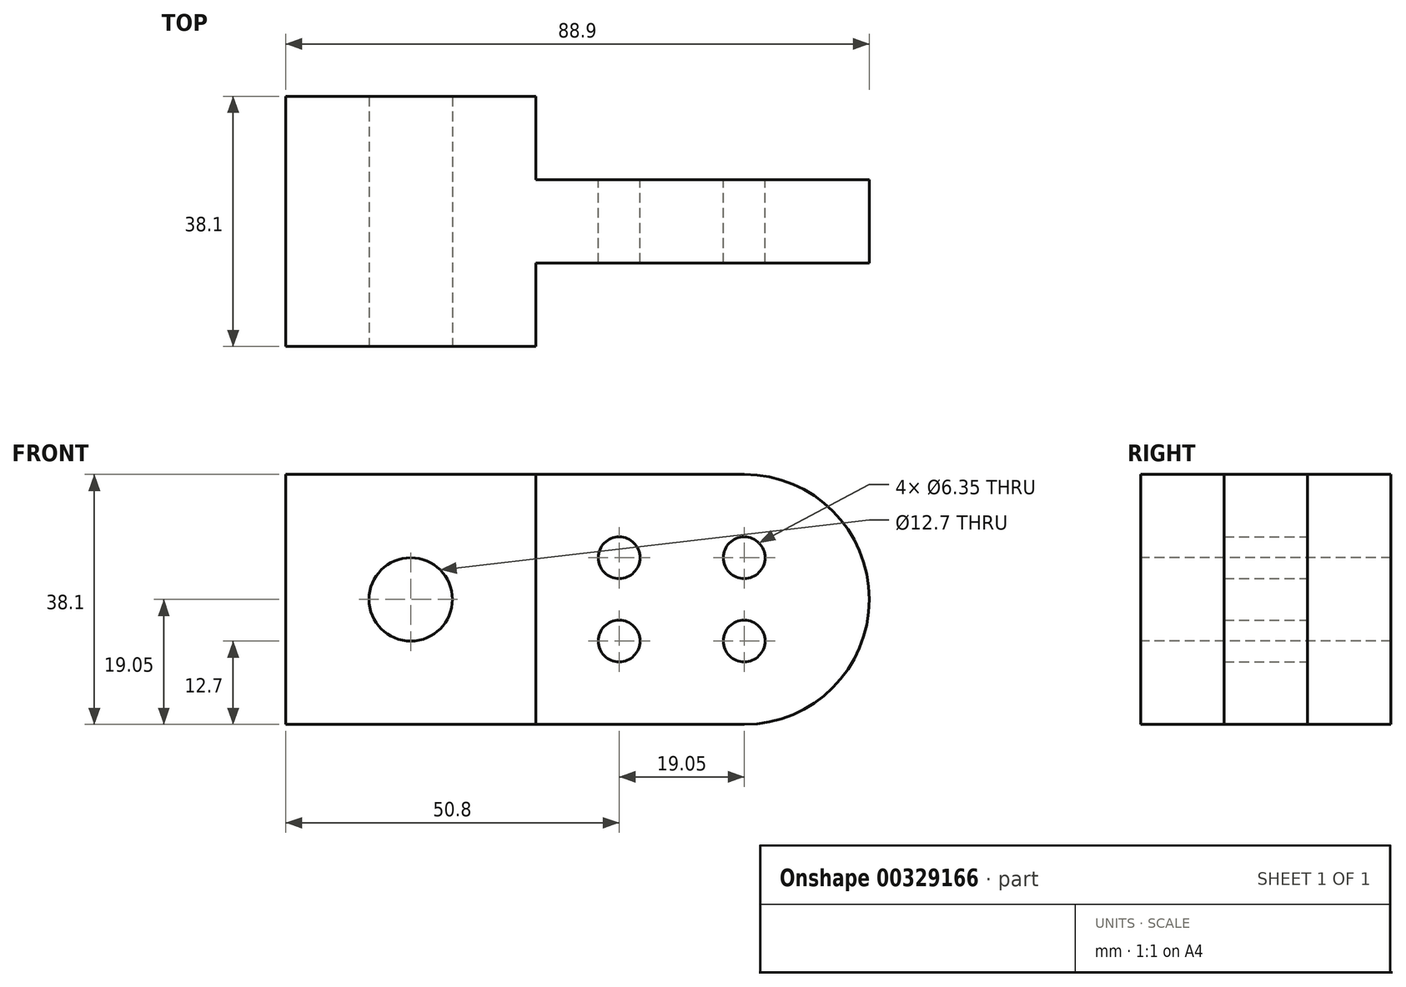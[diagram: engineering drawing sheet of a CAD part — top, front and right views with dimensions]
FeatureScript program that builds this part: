
annotation { "Feature Type Name" : "Feature", "Feature Type Description" : "" }
export const myFeature = defineFeature(function(context is Context, id is Id, definition is map)
    precondition{}
    {
        {
            var Q0;
            Q0=qCreatedBy(makeId("Front.planeOp"),FACE);
            var sketch = newSketch(context, id + "F0", { "sketchPlane" : qUnion([Q0])});
            skLineSegment(sketch, "E0", {"start": v(0, 0) * mm, "end": v(0, 38.1) * mm});
            skLineSegment(sketch, "E1", {"start": v(0, 38.1) * mm, "end": v(38.1, 38.1) * mm});
            skLineSegment(sketch, "E2", {"start": v(38.1, 38.1) * mm, "end": v(38.1, 0) * mm});
            skLineSegment(sketch, "E3", {"start": v(38.1, 0) * mm, "end": v(0, 0) * mm});
            skLineSegment(sketch, "E4", {"start": v(38.1, 38.1) * mm, "end": v(69.85, 38.1) * mm});
            skLineSegment(sketch, "E5", {"start": v(38.1, 0) * mm, "end": v(69.85, 0) * mm});
            skArc(sketch, "E6", {"start": v(69.85, 0) * mm, "mid": v(88.9, 19.05) * mm, "end": v(69.85, 38.1) * mm});
            skLineSegment(sketch, "E7", {"start": v(38.1, 25.4) * mm, "end": v(109.02, 25.4) * mm, "construction": true});
            skLineSegment(sketch, "E8", {"start": v(38.1, 12.7) * mm, "end": v(109.02, 12.7) * mm, "construction": true});
            skLineSegment(sketch, "E9", {"start": v(38.1, 19.05) * mm, "end": v(88.9, 19.05) * mm});
            skLineSegment(sketch, "E10", {"start": v(50.8, 38.1) * mm, "end": v(50.8, 0) * mm, "construction": true});
            skLineSegment(sketch, "E11", {"start": v(69.85, 38.1) * mm, "end": v(69.85, 0) * mm, "construction": true});
            skCircle(sketch, "E12", {"center": v(50.8, 25.4) * mm, "radius": 3.18 * mm});
            skCircle(sketch, "E13", {"center": v(69.85, 25.4) * mm, "radius": 3.18 * mm});
            skCircle(sketch, "E14", {"center": v(69.85, 12.7) * mm, "radius": 3.18 * mm});
            skCircle(sketch, "E15", {"center": v(50.8, 12.7) * mm, "radius": 3.18 * mm});
            skSolve(sketch);
        }
        {
            var Q0;
            Q0=makeQuery(id+"F0.imprint","IMPRINT",FACE,{"disambiguationData":[TD([[makeQuery(id+"F0.imprint","IMPRINT",EDGE,{"derivedFrom":sQuery(id+"F0.wireOp",EDGE,"E0")}),-1.0]])]});
            var Q1;
            {var subQ2=sQuery(id+"F0.wireOp",EDGE,"E4");Q1=makeQuery(id+"F0.imprint","IMPRINT",FACE,{"disambiguationData":[TD([[makeQuery(id+"F0.imprint","IMPRINT",EDGE,{"derivedFrom":subQ2}),-1.0]])]});}
            var Q2;
            {var subQ2=sQuery(id+"F0.wireOp",EDGE,"E5");Q2=makeQuery(id+"F0.imprint","IMPRINT",FACE,{"disambiguationData":[TD([[makeQuery(id+"F0.imprint","IMPRINT",EDGE,{"derivedFrom":subQ2}),1.0]])]});}
            extrude(context, id + "F1", {"entities" : qUnion([Q0, Q1, Q2]), "depth" : 38.1 * mm});
        }
        {
            var Q0;
            Q0=qCreatedBy(makeId("Top.planeOp"),FACE);
            var sketch = newSketch(context, id + "F2", { "sketchPlane" : qUnion([Q0])});
            skLineSegment(sketch, "E16", {"start": v(0, 0) * mm, "end": v(38.1, 0) * mm});
            skLineSegment(sketch, "E17", {"start": v(38.1, 0) * mm, "end": v(38.1, -12.7) * mm});
            skLineSegment(sketch, "E18", {"start": v(38.1, -12.7) * mm, "end": v(88.9, -12.7) * mm});
            skLineSegment(sketch, "E19", {"start": v(88.9, -12.7) * mm, "end": v(88.9, -25.4) * mm});
            skLineSegment(sketch, "E20", {"start": v(88.9, -25.4) * mm, "end": v(38.1, -25.4) * mm});
            skLineSegment(sketch, "E21", {"start": v(38.1, -25.4) * mm, "end": v(38.1, -38.1) * mm});
            skLineSegment(sketch, "E22", {"start": v(38.1, -38.1) * mm, "end": v(0, -38.1) * mm});
            skLineSegment(sketch, "E23", {"start": v(0, -38.1) * mm, "end": v(0, 0) * mm});
            skLineSegment(sketch, "E24", {"start": v(38.1, -38.1) * mm, "end": v(88.9, -38.1) * mm});
            skLineSegment(sketch, "E25", {"start": v(88.9, -12.7) * mm, "end": v(88.9, 0) * mm});
            skLineSegment(sketch, "E26", {"start": v(88.9, 0) * mm, "end": v(38.1, 0) * mm});
            skLineSegment(sketch, "E27", {"start": v(88.9, -38.1) * mm, "end": v(88.9, -25.4) * mm});
            skSolve(sketch);
        }
        {
            var Q0;
            Q0=makeQuery(id+"F2.imprint","IMPRINT",FACE,{"disambiguationData":[TD([[makeQuery(id+"F2.imprint","IMPRINT",EDGE,{"derivedFrom":sQuery(id+"F2.wireOp",EDGE,"E17")}),1.0]])]});
            var Q1;
            Q1=makeQuery(id+"F2.imprint","IMPRINT",FACE,{"disambiguationData":[TD([[makeQuery(id+"F2.imprint","IMPRINT",EDGE,{"derivedFrom":sQuery(id+"F2.wireOp",EDGE,"E20")}),1.0]])]});
            var Q2;
            Q2=makeQuery(id+"F2.imprint","IMPRINT",FACE,{"disambiguationData":[TD([[makeQuery(id+"F2.imprint","IMPRINT",EDGE,{"derivedFrom":sQuery(id+"F2.wireOp",EDGE,"E17")}),1.0]])]});
            var Q3;
            Q3=makeQuery(id+"F2.imprint","IMPRINT",FACE,{"disambiguationData":[TD([[makeQuery(id+"F2.imprint","IMPRINT",EDGE,{"derivedFrom":sQuery(id+"F2.wireOp",EDGE,"E20")}),1.0]])]});
            extrude(context, id + "F3", {"entities" : qUnion([Q0, Q1, Q2, Q3]), "operationType" : NewBodyOperationType.REMOVE, "endBound" : BoundingType.THROUGH_ALL, "depth" : 25.4 * mm});
        }
        {
            var Q0;
            Q0=makeQuery(id+"F1.opExtrude","CAP_FACE",FACE,{"disambiguationData":[OSD([sQuery(id+"F0.wireOp",EDGE,"E0"),sQuery(id+"F0.wireOp",EDGE,"E1"),sQuery(id+"F0.wireOp",EDGE,"E3"),sQuery(id+"F0.wireOp",EDGE,"E4"),sQuery(id+"F0.wireOp",EDGE,"E5"),sQuery(id+"F0.wireOp",EDGE,"E6"),sQuery(id+"F0.wireOp",EDGE,"E12"),sQuery(id+"F0.wireOp",EDGE,"E13"),sQuery(id+"F0.wireOp",EDGE,"E14"),sQuery(id+"F0.wireOp",EDGE,"E15")])],"isStart":false});
            var sketch = newSketch(context, id + "F4", { "sketchPlane" : qUnion([Q0])});
            skCircle(sketch, "E28", {"center": v(19.05, 19.05) * mm, "radius": 6.35 * mm});
            skPoint(sketch, "E28.centerSnap0", {"position": v(0, 19.05) * mm});
            skPoint(sketch, "E28.centerSnap1", {"position": v(19.05, 38.1) * mm});
            skSolve(sketch);
        }
        {
            var Q0;
            Q0=makeQuery(id+"F4.imprint","IMPRINT",FACE,{"disambiguationData":[TD([[makeQuery(id+"F4.imprint","IMPRINT",EDGE,{"derivedFrom":sQuery(id+"F4.wireOp",EDGE,"E28")}),1.0]])]});
            extrude(context, id + "F5", {"entities" : qUnion([Q0]), "operationType" : NewBodyOperationType.REMOVE, "endBound" : BoundingType.THROUGH_ALL, "oppositeDirection" : true, "depth" : 25.4 * mm});
        }
    });
